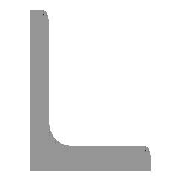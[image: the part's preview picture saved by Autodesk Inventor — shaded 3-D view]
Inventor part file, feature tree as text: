
AUTODESK INVENTOR PART (.ipt)
format: ipt  version: 2023.4 (Build 274418000, 418)  size: 122,368 bytes
history: native  units: mm (DEFAULTED — no unit token found)
features: other x3, sketch x1, plane x1
ambient origin geometry x8: Origin, YZ Plane, XZ Plane, XY Plane, X Axis, Y Axis, Z Axis, Center Point
bodies: Solid1 (feature_tree), Body (feature_tree)
feature tree (5):
  other  "Driven Length"
  other  "Start plane"
  other  "End plane"
  sketch  "Sketch3"  dims[d0=25.4mm d1=25.4mm d2=3.175mm d3=3.175mm d4=25.4mm d5=0.0mm d10=0.0mm d11=0.0mm d12=-0.0mm d13=25.4mm d14=3.302mm d15=1.524mm d16=90.0deg d17=25.4mm]
  plane  "Work Plane3"
